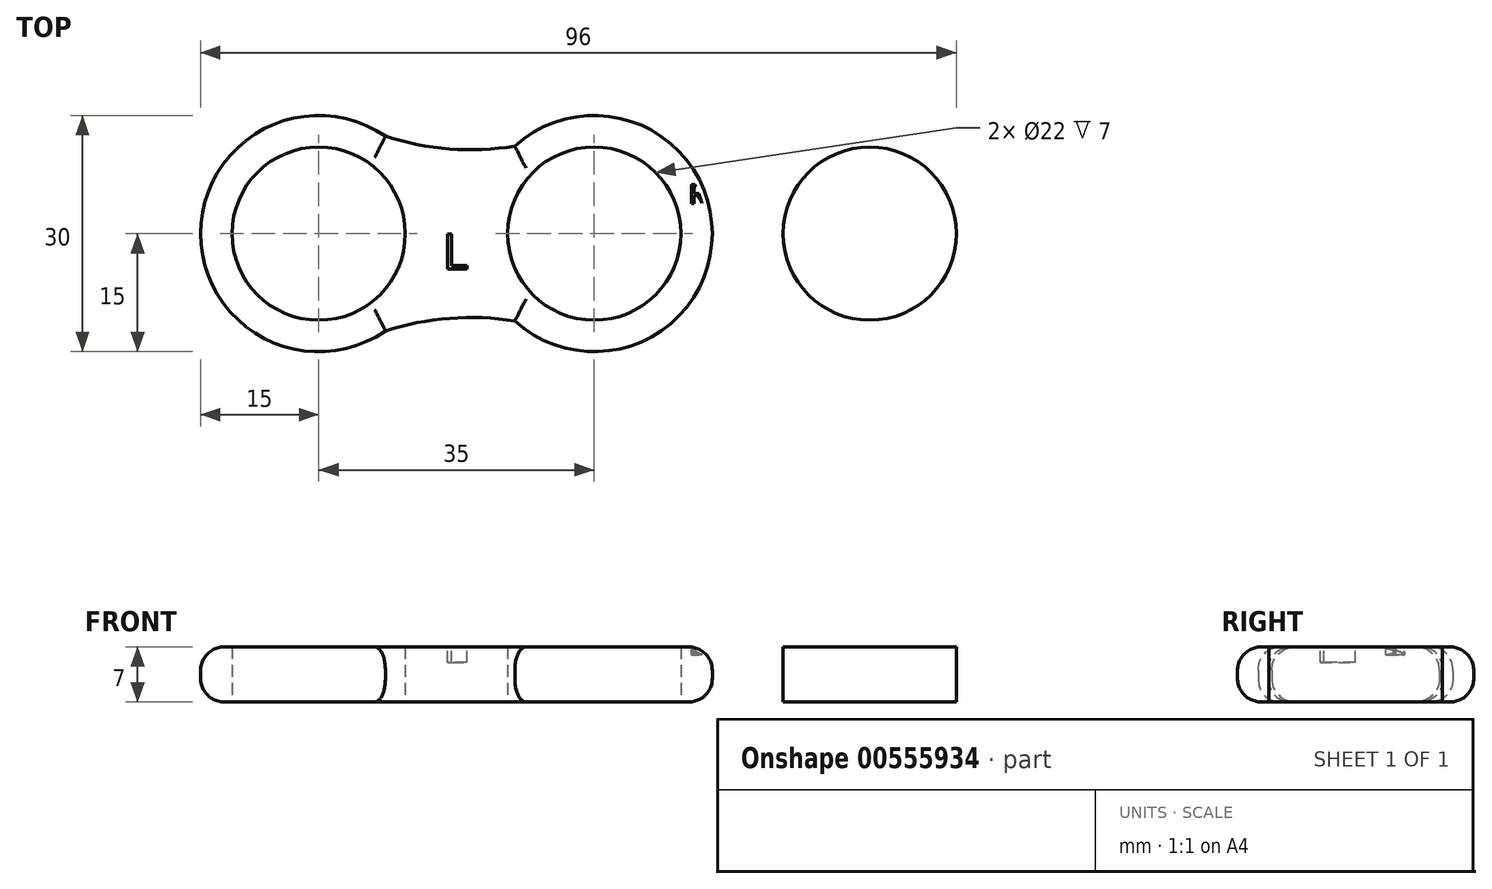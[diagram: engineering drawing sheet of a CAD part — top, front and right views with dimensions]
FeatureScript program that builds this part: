
annotation { "Feature Type Name" : "Feature", "Feature Type Description" : "" }
export const myFeature = defineFeature(function(context is Context, id is Id, definition is map)
    precondition{}
    {
        {
            var Q0;
            Q0=qCreatedBy(makeId("Top.planeOp"),FACE);
            var sketch = newSketch(context, id + "F0", { "sketchPlane" : qUnion([Q0])});
            skPoint(sketch, "E0.middle", {"position": v(0, 0) * mm});
            skCircle(sketch, "E1", {"center": v(0, 0) * mm, "radius": 11 * mm});
            skCircle(sketch, "E2", {"center": v(0, 0) * mm, "radius": 15 * mm});
            skCircle(sketch, "E3", {"center": v(-35, 0) * mm, "radius": 11 * mm});
            skCircle(sketch, "E4", {"center": v(-35, 0) * mm, "radius": 15 * mm});
            skArc(sketch, "E5", {"start": v(-26.52, 12.37) * mm, "mid": v(-18.37, 10.76) * mm, "end": v(-10.08, 11.11) * mm});
            skArc(sketch, "E6.MirrorCS", {"start": v(-26.52, -12.37) * mm, "mid": v(-18.37, -10.76) * mm, "end": v(-10.08, -11.11) * mm});
            skArc(sketch, "E7.MirrorCS", {"start": v(26.52, 12.37) * mm, "mid": v(18.37, 10.76) * mm, "end": v(10.08, 11.11) * mm});
            skArc(sketch, "E8.MirrorCS", {"start": v(26.52, -12.37) * mm, "mid": v(18.37, -10.76) * mm, "end": v(10.08, -11.11) * mm});
            skCircle(sketch, "E9.MirrorC", {"center": v(35, 0) * mm, "radius": 15 * mm});
            skCircle(sketch, "E10.MirrorC", {"center": v(35, 0) * mm, "radius": 11 * mm});
            skSolve(sketch);
        }
        {
            var Q0;
            Q0=makeQuery(id+"F0.imprint","IMPRINT",FACE,{"disambiguationData":[TD([[makeQuery(id+"F0.imprint","IMPRINT",EDGE,{"derivedFrom":sQuery(id+"F0.wireOp",EDGE,"cd22e090-de5e-44ce-a2e8-da55deea97581.MirrorC")}),1.0]])]});
            var Q1;
            Q1=makeQuery(id+"F0.imprint","IMPRINT",FACE,{"disambiguationData":[TD([[makeQuery(id+"F0.imprint","IMPRINT",EDGE,{"derivedFrom":sQuery(id+"F0.wireOp",EDGE,"E1")}),-1.0]])]});
            var Q2;
            {var subQ0=sQuery(id+"F0.wireOp",EDGE,"e8e17bcd-66d5-45fb-b403-fcb8348c6d070.MirrorCS");Q2=makeQuery(id+"F0.imprint","IMPRINT",FACE,{"disambiguationData":[TD([[makeQuery(id+"F0.imprint","IMPRINT",EDGE,{"derivedFrom":subQ0}),-1.0]])]});}
            var Q3;
            {var subQ0=sQuery(id+"F0.wireOp",EDGE,"E5");Q3=makeQuery(id+"F0.imprint","IMPRINT",FACE,{"disambiguationData":[TD([[makeQuery(id+"F0.imprint","IMPRINT",EDGE,{"derivedFrom":subQ0}),-1.0]])]});}
            var Q4;
            Q4=makeQuery(id+"F0.imprint","IMPRINT",FACE,{"disambiguationData":[TD([[makeQuery(id+"F0.imprint","IMPRINT",EDGE,{"derivedFrom":sQuery(id+"F0.wireOp",EDGE,"E3")}),-1.0]])]});
            var Q5;
            Q5=makeQuery(id+"F0.imprint","IMPRINT",FACE,{"disambiguationData":[TD([[makeQuery(id+"F0.imprint","IMPRINT",EDGE,{"derivedFrom":sQuery(id+"F0.wireOp",EDGE,"E10.MirrorC")}),1.0]])]});
            var Q6;
            {var subQ0=sQuery(id+"F0.wireOp",EDGE,"E7.MirrorCS");Q6=makeQuery(id+"F0.imprint","IMPRINT",FACE,{"disambiguationData":[TD([[makeQuery(id+"F0.imprint","IMPRINT",EDGE,{"derivedFrom":subQ0}),1.0]])]});}
            extrude(context, id + "F1", {"entities" : qUnion([Q0, Q1, Q2, Q3, Q4, Q5, Q6]), "depth" : 7 * mm});
        }
        {
            var Q0;
            Q0=makeQuery(id+"F1.opExtrude","CAP_EDGE",EDGE,{"disambiguationData":[OSD([sQuery(id+"F0.wireOp",EDGE,"E5")])],"isStart":true});
            var Q1;
            Q1=makeQuery(id+"F1.opExtrude","CAP_EDGE",EDGE,{"disambiguationData":[OSD([sQuery(id+"F0.wireOp",EDGE,"E4")])],"isStart":true});
            var Q2;
            Q2=makeQuery(id+"F1.opExtrude","CAP_EDGE",EDGE,{"disambiguationData":[OSD([sQuery(id+"F0.wireOp",EDGE,"E6.MirrorCS")])],"isStart":true});
            var Q3;
            {var subQ0=sQuery(id+"F0.wireOp",EDGE,"E2");Q3=makeQuery(id+"F1.opExtrude","CAP_EDGE",EDGE,{"disambiguationData":[OSD([subQ0]),TDD([makeQuery(id+"F0.imprint","IMPRINT",EDGE,{"disambiguationData":[TD([[makeQuery(id+"F0.imprint","INTERSECT",VERTEX,{"derivedFrom":[subQ0,sQuery(id+"F0.wireOp",EDGE,"E6.MirrorCS")]}),-1.0]])],"derivedFrom":subQ0})])],"isStart":true});}
            var Q4;
            Q4=makeQuery(id+"F1.opExtrude","CAP_EDGE",EDGE,{"disambiguationData":[OSD([sQuery(id+"F0.wireOp",EDGE,"E8.MirrorCS")])],"isStart":true});
            var Q5;
            Q5=makeQuery(id+"F1.opExtrude","CAP_EDGE",EDGE,{"disambiguationData":[OSD([sQuery(id+"F0.wireOp",EDGE,"E9.MirrorC")])],"isStart":true});
            var Q6;
            Q6=makeQuery(id+"F1.opExtrude","CAP_EDGE",EDGE,{"disambiguationData":[OSD([sQuery(id+"F0.wireOp",EDGE,"E7.MirrorCS")])],"isStart":true});
            var Q7;
            {var subQ0=sQuery(id+"F0.wireOp",EDGE,"E2");Q7=makeQuery(id+"F1.opExtrude","CAP_EDGE",EDGE,{"disambiguationData":[OSD([subQ0]),TDD([makeQuery(id+"F0.imprint","IMPRINT",EDGE,{"disambiguationData":[TD([[makeQuery(id+"F0.imprint","INTERSECT",VERTEX,{"derivedFrom":[subQ0,sQuery(id+"F0.wireOp",EDGE,"E5")]}),1.0]])],"derivedFrom":subQ0})])],"isStart":true});}
            fillet(context, id + "F2", {"entities" : qUnion([Q0, Q1, Q2, Q3, Q4, Q5, Q6, Q7]), "radius" : 3 * mm, "tangentPropagation" : true, "allowEdgeOverflow" : false});
        }
        {
            var Q0;
            Q0=makeQuery(id+"F1.opExtrude","CAP_EDGE",EDGE,{"disambiguationData":[OSD([sQuery(id+"F0.wireOp",EDGE,"E9.MirrorC")])],"isStart":false});
            var Q1;
            Q1=makeQuery(id+"F1.opExtrude","CAP_EDGE",EDGE,{"disambiguationData":[OSD([sQuery(id+"F0.wireOp",EDGE,"E8.MirrorCS")])],"isStart":false});
            var Q2;
            {var subQ0=sQuery(id+"F0.wireOp",EDGE,"E2");Q2=makeQuery(id+"F1.opExtrude","CAP_EDGE",EDGE,{"disambiguationData":[OSD([subQ0]),TDD([makeQuery(id+"F0.imprint","IMPRINT",EDGE,{"disambiguationData":[TD([[makeQuery(id+"F0.imprint","INTERSECT",VERTEX,{"derivedFrom":[subQ0,sQuery(id+"F0.wireOp",EDGE,"E6.MirrorCS")]}),-1.0]])],"derivedFrom":subQ0})])],"isStart":false});}
            var Q3;
            Q3=makeQuery(id+"F1.opExtrude","CAP_EDGE",EDGE,{"disambiguationData":[OSD([sQuery(id+"F0.wireOp",EDGE,"E6.MirrorCS")])],"isStart":false});
            var Q4;
            Q4=makeQuery(id+"F1.opExtrude","CAP_EDGE",EDGE,{"disambiguationData":[OSD([sQuery(id+"F0.wireOp",EDGE,"E4")])],"isStart":false});
            var Q5;
            Q5=makeQuery(id+"F1.opExtrude","CAP_EDGE",EDGE,{"disambiguationData":[OSD([sQuery(id+"F0.wireOp",EDGE,"E5")])],"isStart":false});
            var Q6;
            {var subQ0=sQuery(id+"F0.wireOp",EDGE,"E2");Q6=makeQuery(id+"F1.opExtrude","CAP_EDGE",EDGE,{"disambiguationData":[OSD([subQ0]),TDD([makeQuery(id+"F0.imprint","IMPRINT",EDGE,{"disambiguationData":[TD([[makeQuery(id+"F0.imprint","INTERSECT",VERTEX,{"derivedFrom":[subQ0,sQuery(id+"F0.wireOp",EDGE,"E5")]}),1.0]])],"derivedFrom":subQ0})])],"isStart":false});}
            var Q7;
            Q7=makeQuery(id+"F1.opExtrude","CAP_EDGE",EDGE,{"disambiguationData":[OSD([sQuery(id+"F0.wireOp",EDGE,"E7.MirrorCS")])],"isStart":false});
            fillet(context, id + "F3", {"entities" : qUnion([Q0, Q1, Q2, Q3, Q4, Q5, Q6, Q7]), "radius" : 3 * mm, "tangentPropagation" : true, "allowEdgeOverflow" : false});
        }
        {
            var Q0;
            Q0=makeQuery(id+"F1.opExtrude","CAP_FACE",FACE,{"disambiguationData":[OSD([sQuery(id+"F0.wireOp",EDGE,"E1"),sQuery(id+"F0.wireOp",EDGE,"E2"),sQuery(id+"F0.wireOp",EDGE,"E3"),sQuery(id+"F0.wireOp",EDGE,"E4"),sQuery(id+"F0.wireOp",EDGE,"E5"),sQuery(id+"F0.wireOp",EDGE,"E6.MirrorCS"),sQuery(id+"F0.wireOp",EDGE,"E7.MirrorCS"),sQuery(id+"F0.wireOp",EDGE,"E8.MirrorCS"),sQuery(id+"F0.wireOp",EDGE,"E9.MirrorC"),sQuery(id+"F0.wireOp",EDGE,"E10.MirrorC")])],"isStart":false});
            var sketch = newSketch(context, id + "F4", { "sketchPlane" : qUnion([Q0])});
            skText(sketch, "E11", { "text": "R.H.K", "fontName": "OpenSans-Regular.ttf"});
            const initialGuessF4  = {"E11": [0.01206, 0.00384, 1, 0, 0.00239]};
            skSetInitialGuess(sketch, initialGuessF4);
            skSolve(sketch);
        }
        {
            var Q0;
            Q0=qSketchRegion(id+"F4",true);
            extrude(context, id + "F5", {"entities" : qUnion([Q0]), "operationType" : NewBodyOperationType.REMOVE, "oppositeDirection" : true, "depth" : 1 * mm});
        }
        {
            var Q0;
            {var subQ0=sQuery(id+"F0.wireOp",EDGE,"E8.MirrorCS");var subQ1=sQuery(id+"F0.wireOp",EDGE,"E7.MirrorCS");var subQ2=sQuery(id+"F0.wireOp",EDGE,"E5");var subQ3=sQuery(id+"F0.wireOp",EDGE,"E4");var subQ4=sQuery(id+"F0.wireOp",EDGE,"E6.MirrorCS");var subQ5=sQuery(id+"F0.wireOp",EDGE,"E2");var subQ6=sQuery(id+"F0.wireOp",EDGE,"E3");var subQ7=sQuery(id+"F0.wireOp",EDGE,"E1");var subQ8=sQuery(id+"F0.wireOp",EDGE,"E9.MirrorC");var subQ9=sQuery(id+"F0.wireOp",EDGE,"E10.MirrorC");Q0=makeQuery(id+"F5.boolean.opBoolean","SPLIT",FACE,{"disambiguationData":[TD([makeQuery(id+"F1.opExtrude","SWEPT_FACE",FACE,{"disambiguationData":[OSD([subQ7])]})])],"derivedFrom":makeQuery(id+"F1.opExtrude","CAP_FACE",FACE,{"disambiguationData":[OSD([subQ7,subQ5,subQ6,subQ3,subQ2,subQ4,subQ1,subQ0,subQ8,subQ9])],"isStart":false})});}
            var sketch = newSketch(context, id + "F6", { "sketchPlane" : qUnion([Q0])});
            skText(sketch, "E12", { "text": "L", "fontName": "OpenSans-Regular.ttf"});
            const initialGuessF6  = {"E12": [-0.01925, -0.0045, 1, 0, 0.0045]};
            skSetInitialGuess(sketch, initialGuessF6);
            skSolve(sketch);
        }
        {
            var Q0;
            Q0=qSketchRegion(id+"F6",true);
            extrude(context, id + "F7", {"entities" : qUnion([Q0]), "operationType" : NewBodyOperationType.REMOVE, "oppositeDirection" : true, "depth" : 2 * mm});
        }
    });
